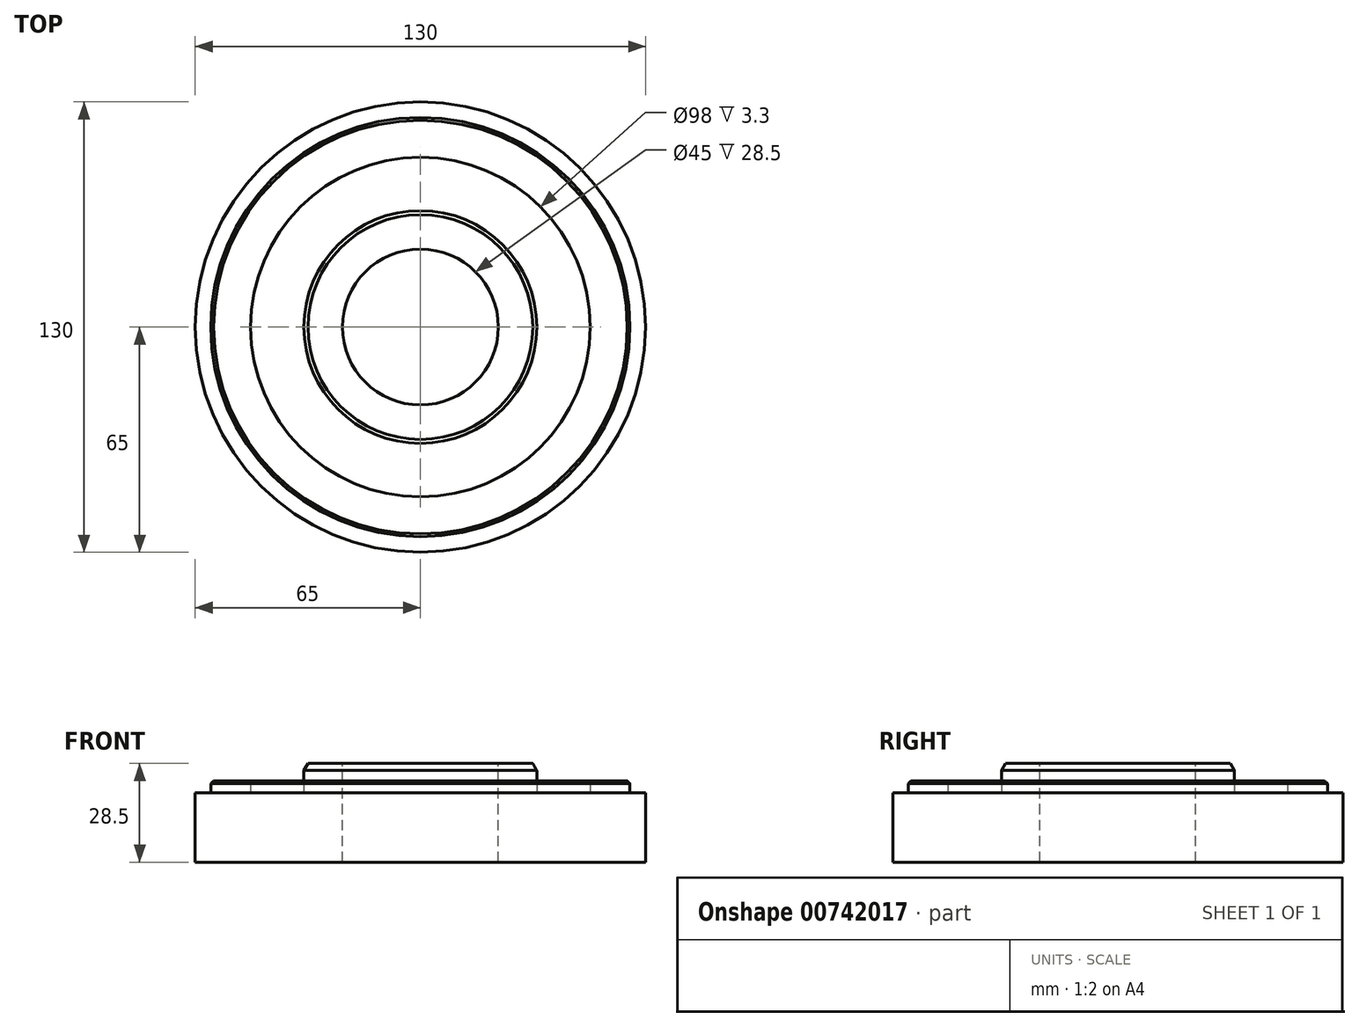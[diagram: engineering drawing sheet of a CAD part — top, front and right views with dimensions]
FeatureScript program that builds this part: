
annotation { "Feature Type Name" : "Feature", "Feature Type Description" : "" }
export const myFeature = defineFeature(function(context is Context, id is Id, definition is map)
    precondition{}
    {
        {
            var Q0;
            Q0=qCreatedBy(makeId("Front.planeOp"),FACE);
            var sketch = newSketch(context, id + "F0", { "sketchPlane" : qUnion([Q0])});
            skLineSegment(sketch, "E0", {"start": v(0, -23.5) * mm, "end": v(65, -23.5) * mm});
            skLineSegment(sketch, "E1", {"start": v(65, -23.5) * mm, "end": v(65, -3.5) * mm});
            skLineSegment(sketch, "E2", {"start": v(65, -3.5) * mm, "end": v(60.5, -3.5) * mm});
            skLineSegment(sketch, "E3", {"start": v(60.5, -3.5) * mm, "end": v(60.5, 0) * mm});
            skLineSegment(sketch, "E4", {"start": v(60.5, 0) * mm, "end": v(49, 0) * mm});
            skLineSegment(sketch, "E5", {"start": v(49, 0) * mm, "end": v(49, -3.3) * mm});
            skLineSegment(sketch, "E6", {"start": v(49, -3.3) * mm, "end": v(33.6, -3.3) * mm});
            skLineSegment(sketch, "E7", {"start": v(33.6, -3.3) * mm, "end": v(33.6, 5) * mm});
            skLineSegment(sketch, "E8", {"start": v(33.6, 5) * mm, "end": v(0, 5) * mm});
            skLineSegment(sketch, "E9", {"start": v(0, 5) * mm, "end": v(0, -23.5) * mm});
            skLineSegment(sketch, "E10", {"start": v(0, 0) * mm, "end": v(0, 40) * mm});
            skSolve(sketch);
        }
        {
            var Q0;
            Q0=makeQuery(id+"F0.imprint","IMPRINT",FACE,{"disambiguationData":[TD([[makeQuery(id+"F0.imprint","IMPRINT",EDGE,{"derivedFrom":sQuery(id+"F0.wireOp",EDGE,"E0")}),1.0]])]});
            var Q1;
            Q1=sQuery(id+"F0.wireOp",EDGE,"E10");
            revolve(context, id + "F1", {"surfaceOperationType" : NewSurfaceOperationType.NEW, "entities" : qUnion([Q0]), "axis" : qUnion([Q1]), "revolveType" : RevolveType.FULL});
        }
        {
            var Q0;
            Q0=makeQuery(id+"F1.opRevolve","SWEPT_EDGE",EDGE,{"disambiguationData":[OSD([sQuery(id+"F0.wireOp",EDGE,"E3"),sQuery(id+"F0.wireOp",EDGE,"E4")])]});
            chamfer(context, id + "F2", {"entities" : qUnion([Q0]), "width" : .81 * mm, "tangentPropagation" : true});
        }
        {
            var Q0;
            Q0=makeQuery(id+"F1.opRevolve","SWEPT_EDGE",EDGE,{"disambiguationData":[OSD([sQuery(id+"F0.wireOp",EDGE,"E7"),sQuery(id+"F0.wireOp",EDGE,"E8")])]});
            chamfer(context, id + "F3", {"entities" : qUnion([Q0]), "chamferType" : ChamferType.OFFSET_ANGLE, "width" : 2 * mm, "oppositeDirection" : false, "angle" : 30 * degree, "tangentPropagation" : true});
        }
        {
            var Q0;
            Q0=makeQuery(id+"F1.opRevolve","SWEPT_FACE",FACE,{"disambiguationData":[OSD([sQuery(id+"F0.wireOp",EDGE,"E8")])]});
            var sketch = newSketch(context, id + "F4", { "sketchPlane" : qUnion([Q0])});
            skCircle(sketch, "E11", {"center": v(0, 0) * mm, "radius": 22.5 * mm});
            skSolve(sketch);
        }
        {
            var Q0;
            Q0 = qSketchRegion(id + "F4", true);
            extrude(context, id + "F5", {"entities" : qUnion([Q0]), "oppositeDirection" : true, "depth" : 50 * mm, "offsetDistance" : 25 * mm, "hasSecondDirection" : true, "secondDirectionOppositeDirection" : false, "secondDirectionDepth" : 16.8 * mm});
        }
        {
            var Q0;
            Q0=makeQuery(id+"F5.opExtrude","SWEPT_BODY",BODY,{"disambiguationData":[OSD([sQuery(id+"F4.wireOp",EDGE,"E11")])]});
            var Q1;
            Q1=makeQuery(id+"F1.opRevolve","SWEPT_BODY",BODY,{"disambiguationData":[OSD([sQuery(id+"F0.wireOp",EDGE,"E0"),sQuery(id+"F0.wireOp",EDGE,"E1"),sQuery(id+"F0.wireOp",EDGE,"E2"),sQuery(id+"F0.wireOp",EDGE,"E3"),sQuery(id+"F0.wireOp",EDGE,"E4"),sQuery(id+"F0.wireOp",EDGE,"E5"),sQuery(id+"F0.wireOp",EDGE,"E6"),sQuery(id+"F0.wireOp",EDGE,"E7"),sQuery(id+"F0.wireOp",EDGE,"E8"),sQuery(id+"F0.wireOp",EDGE,"E9"),sQuery(id+"F0.wireOp",EDGE,"E10")])]});
            booleanBodies(context, id + "F6", {"operationType" : BooleanOperationType.SUBTRACTION, "tools" : qUnion([Q0]), "targets" : qUnion([Q1])});
        }
    });
